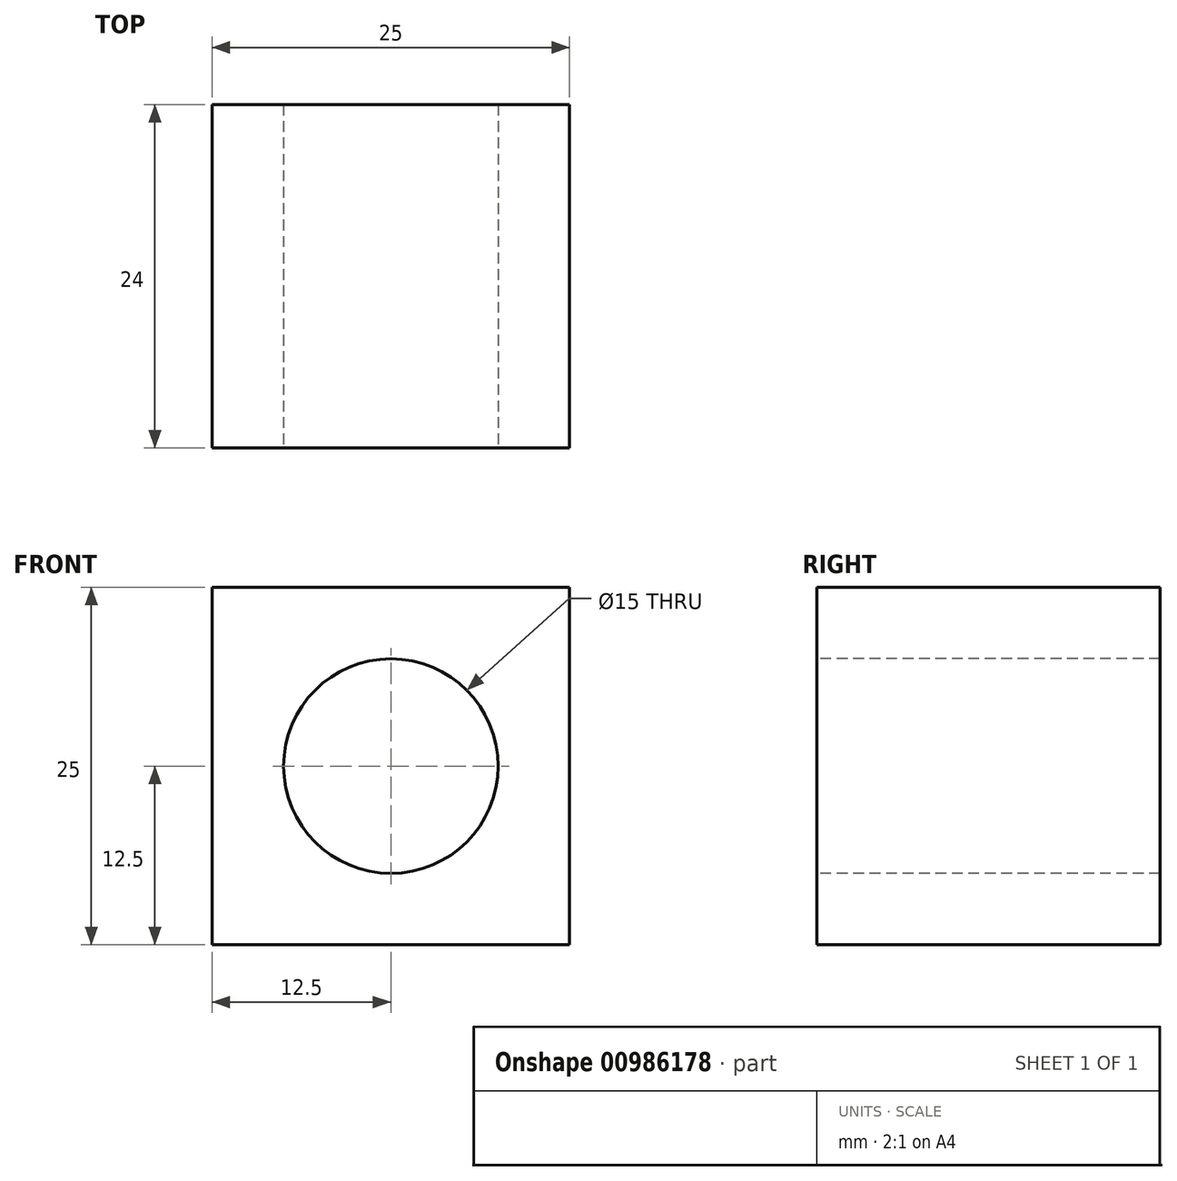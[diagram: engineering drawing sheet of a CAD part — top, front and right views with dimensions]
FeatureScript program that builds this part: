
annotation { "Feature Type Name" : "Feature", "Feature Type Description" : "" }
export const myFeature = defineFeature(function(context is Context, id is Id, definition is map)
    precondition{}
    {
        {
            var Q0;
            Q0=qCreatedBy(makeId("Front.planeOp"),FACE);
            var sketch = newSketch(context, id + "F0", { "sketchPlane" : qUnion([Q0])});
            skLineSegment(sketch, "E0.bottom", {"start": v(125, 165.42) * mm, "end": v(-125, 165.42) * mm});
            skLineSegment(sketch, "E0.top", {"start": v(125, -165.42) * mm, "end": v(-125, -165.42) * mm});
            skLineSegment(sketch, "E0.left", {"start": v(125, 165.42) * mm, "end": v(125, -165.42) * mm});
            skLineSegment(sketch, "E0.right", {"start": v(-125, 165.42) * mm, "end": v(-125, -165.42) * mm});
            skLineSegment(sketch, "E1.bottom", {"start": v(12.5, -12.5) * mm, "end": v(-12.5, -12.5) * mm});
            skLineSegment(sketch, "E1.top", {"start": v(12.5, 12.5) * mm, "end": v(-12.5, 12.5) * mm});
            skLineSegment(sketch, "E1.left", {"start": v(12.5, -12.5) * mm, "end": v(12.5, 12.5) * mm});
            skLineSegment(sketch, "E1.right", {"start": v(-12.5, -12.5) * mm, "end": v(-12.5, 12.5) * mm});
            skPoint(sketch, "E1.middle", {"position": v(0, 0) * mm});
            skSolve(sketch);
        }
        {
            var Q0;
            Q0=makeQuery(id+"F0.imprint","IMPRINT",FACE,{"disambiguationData":[TD([[makeQuery(id+"F0.imprint","IMPRINT",EDGE,{"derivedFrom":sQuery(id+"F0.wireOp",EDGE,"E1.bottom")}),-1.0]])]});
            extrude(context, id + "F1", {"entities" : qUnion([Q0]), "oppositeDirection" : true, "depth" : 24 * mm, "offsetDistance" : 25.4 * mm});
        }
        {
            var Q0;
            Q0=qCreatedBy(makeId("Front.planeOp"),FACE);
            var sketch = newSketch(context, id + "F2", { "sketchPlane" : qUnion([Q0])});
            skCircle(sketch, "E2", {"center": v(0, 0) * mm, "radius": 7.5 * mm});
            skSolve(sketch);
        }
        {
            var Q0;
            Q0=makeQuery(id+"F2.imprint","IMPRINT",FACE,{"disambiguationData":[TD([[makeQuery(id+"F2.imprint","IMPRINT",EDGE,{"derivedFrom":sQuery(id+"F2.wireOp",EDGE,"E2")}),1.0]])]});
            extrude(context, id + "F3", {"entities" : qUnion([Q0]), "operationType" : NewBodyOperationType.REMOVE, "oppositeDirection" : true, "depth" : 28 * mm, "offsetDistance" : 25.4 * mm});
        }
    });
